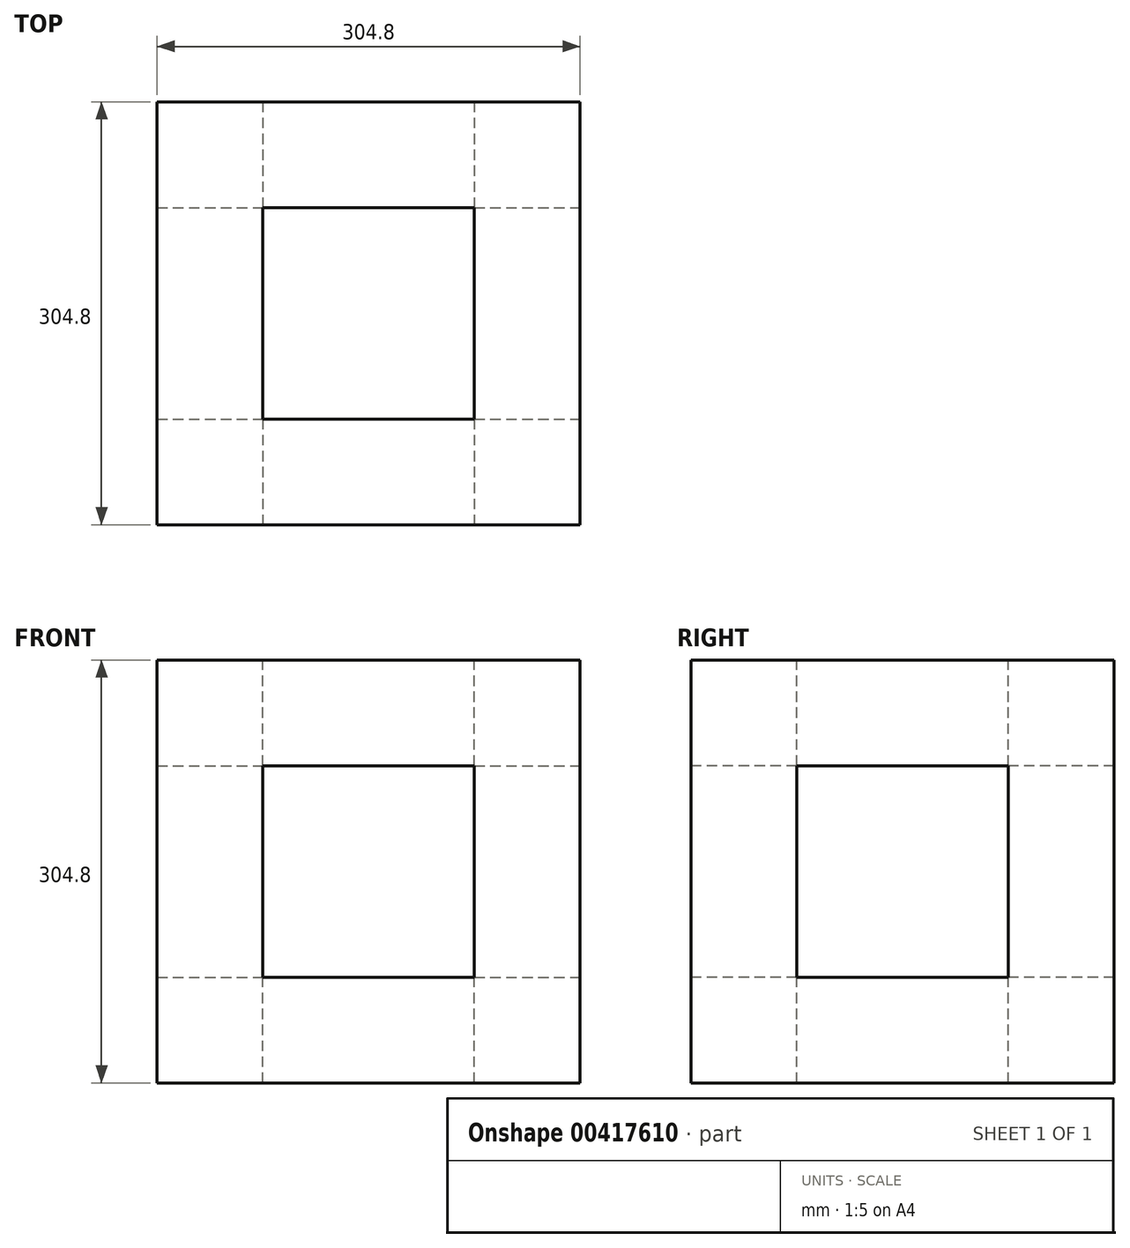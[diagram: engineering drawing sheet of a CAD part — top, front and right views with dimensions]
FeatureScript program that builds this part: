
annotation { "Feature Type Name" : "Feature", "Feature Type Description" : "" }
export const myFeature = defineFeature(function(context is Context, id is Id, definition is map)
    precondition{}
    {
        {
            var Q0;
            Q0=qCreatedBy(makeId("Front.planeOp"),FACE);
            var sketch = newSketch(context, id + "F0", { "sketchPlane" : qUnion([Q0])});
            skLineSegment(sketch, "E0.bottom", {"start": v(-152.4, 152.4) * mm, "end": v(152.4, 152.4) * mm});
            skLineSegment(sketch, "E0.top", {"start": v(-152.4, -152.4) * mm, "end": v(152.4, -152.4) * mm});
            skLineSegment(sketch, "E0.left", {"start": v(-152.4, 152.4) * mm, "end": v(-152.4, -152.4) * mm});
            skLineSegment(sketch, "E0.right", {"start": v(152.4, 152.4) * mm, "end": v(152.4, -152.4) * mm});
            skPoint(sketch, "E0.middle", {"position": v(0, 0) * mm});
            skSolve(sketch);
        }
        {
            var Q0;
            Q0 = qSketchRegion(id + "F0", true);
            extrude(context, id + "F1", {"entities" : qUnion([Q0]), "endBound" : BoundingType.SYMMETRIC, "depth" : 304.8 * mm});
        }
        {
            var Q0;
            Q0=makeQuery(id+"F1.opExtrude","CAP_FACE",FACE,{"disambiguationData":[OSD([sQuery(id+"F0.wireOp",EDGE,"E0.bottom"),sQuery(id+"F0.wireOp",EDGE,"E0.top"),sQuery(id+"F0.wireOp",EDGE,"E0.left"),sQuery(id+"F0.wireOp",EDGE,"E0.right")])],"isStart":false});
            var sketch = newSketch(context, id + "F2", { "sketchPlane" : qUnion([Q0])});
            skLineSegment(sketch, "E1.bottom", {"start": v(-76.2, 76.2) * mm, "end": v(76.2, 76.2) * mm});
            skLineSegment(sketch, "E1.top", {"start": v(-76.2, -76.2) * mm, "end": v(76.2, -76.2) * mm});
            skLineSegment(sketch, "E1.left", {"start": v(-76.2, 76.2) * mm, "end": v(-76.2, -76.2) * mm});
            skLineSegment(sketch, "E1.right", {"start": v(76.2, 76.2) * mm, "end": v(76.2, -76.2) * mm});
            skPoint(sketch, "E1.middle", {"position": v(0, 0) * mm});
            skSolve(sketch);
        }
        {
            var Q0;
            Q0 = qSketchRegion(id + "F2", true);
            extrude(context, id + "F3", {"entities" : qUnion([Q0]), "operationType" : NewBodyOperationType.REMOVE, "endBound" : BoundingType.THROUGH_ALL, "oppositeDirection" : true, "depth" : 25.4 * mm});
        }
        {
            var Q0;
            Q0=makeQuery(id+"F1.opExtrude","SWEPT_FACE",FACE,{"disambiguationData":[OSD([sQuery(id+"F0.wireOp",EDGE,"E0.bottom")])]});
            var sketch = newSketch(context, id + "F4", { "sketchPlane" : qUnion([Q0])});
            skLineSegment(sketch, "E2.bottom", {"start": v(-76.2, -76.2) * mm, "end": v(76.2, -76.2) * mm});
            skLineSegment(sketch, "E2.top", {"start": v(-76.2, 76.2) * mm, "end": v(76.2, 76.2) * mm});
            skLineSegment(sketch, "E2.left", {"start": v(-76.2, -76.2) * mm, "end": v(-76.2, 76.2) * mm});
            skLineSegment(sketch, "E2.right", {"start": v(76.2, -76.2) * mm, "end": v(76.2, 76.2) * mm});
            skPoint(sketch, "E2.middle", {"position": v(0, 0) * mm});
            skSolve(sketch);
        }
        {
            var Q0;
            Q0 = qSketchRegion(id + "F4", true);
            extrude(context, id + "F5", {"entities" : qUnion([Q0]), "operationType" : NewBodyOperationType.REMOVE, "endBound" : BoundingType.THROUGH_ALL, "oppositeDirection" : true, "depth" : 25.4 * mm});
        }
        {
            var Q0;
            Q0=makeQuery(id+"F1.opExtrude","SWEPT_FACE",FACE,{"disambiguationData":[OSD([sQuery(id+"F0.wireOp",EDGE,"E0.right")])]});
            var sketch = newSketch(context, id + "F6", { "sketchPlane" : qUnion([Q0])});
            skLineSegment(sketch, "E3.bottom", {"start": v(-76.2, 76.2) * mm, "end": v(76.2, 76.2) * mm});
            skLineSegment(sketch, "E3.top", {"start": v(-76.2, -76.2) * mm, "end": v(76.2, -76.2) * mm});
            skLineSegment(sketch, "E3.left", {"start": v(-76.2, 76.2) * mm, "end": v(-76.2, -76.2) * mm});
            skLineSegment(sketch, "E3.right", {"start": v(76.2, 76.2) * mm, "end": v(76.2, -76.2) * mm});
            skPoint(sketch, "E3.middle", {"position": v(0, 0) * mm});
            skSolve(sketch);
        }
        {
            var Q0;
            Q0 = qSketchRegion(id + "F6", true);
            extrude(context, id + "F7", {"entities" : qUnion([Q0]), "operationType" : NewBodyOperationType.REMOVE, "endBound" : BoundingType.THROUGH_ALL, "oppositeDirection" : true, "depth" : 25.4 * mm});
        }
    });
